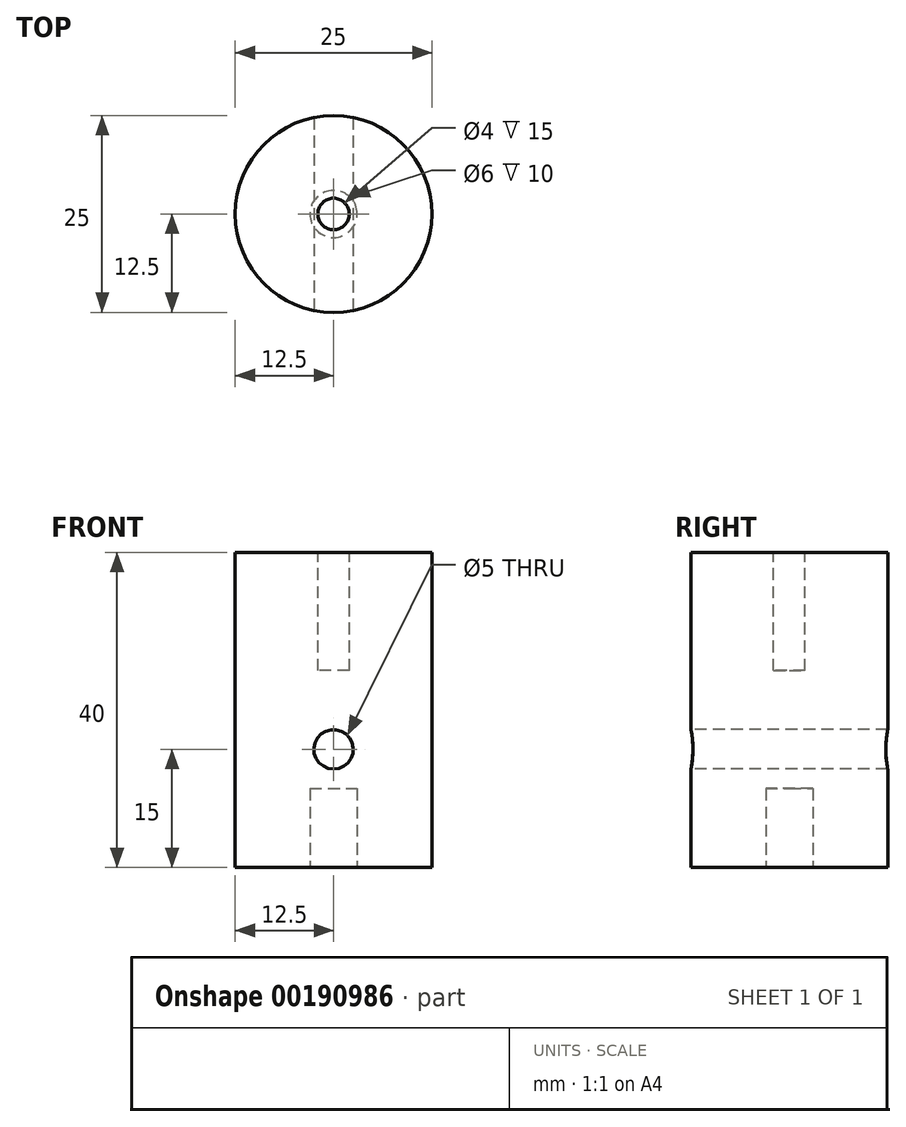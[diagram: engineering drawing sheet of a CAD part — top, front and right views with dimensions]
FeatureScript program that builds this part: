
annotation { "Feature Type Name" : "Feature", "Feature Type Description" : "" }
export const myFeature = defineFeature(function(context is Context, id is Id, definition is map)
    precondition{}
    {
        {
            var Q0;
            Q0=qCreatedBy(makeId("Top.planeOp"),FACE);
            var sketch = newSketch(context, id + "F0", { "sketchPlane" : qUnion([Q0])});
            skCircle(sketch, "E0", {"center": v(0, 0) * mm, "radius": 12.5 * mm});
            skSolve(sketch);
        }
        {
            var Q0;
            Q0 = qSketchRegion(id + "F0", true);
            extrude(context, id + "F1", {"entities" : qUnion([Q0]), "depth" : 40 * mm});
        }
        {
            var Q0;
            Q0=makeQuery(id+"F1.opExtrude","CAP_FACE",FACE,{"disambiguationData":[OSD([sQuery(id+"F0.wireOp",EDGE,"E0")])],"isStart":false});
            var sketch = newSketch(context, id + "F2", { "sketchPlane" : qUnion([Q0])});
            skCircle(sketch, "E1", {"center": v(0, 0) * mm, "radius": 2 * mm});
            skSolve(sketch);
        }
        {
            var Q0;
            Q0 = qSketchRegion(id + "F2", true);
            extrude(context, id + "F3", {"entities" : qUnion([Q0]), "operationType" : NewBodyOperationType.REMOVE, "oppositeDirection" : true, "depth" : 15 * mm});
        }
        {
            var Q0;
            Q0=makeQuery(id+"F1.opExtrude","CAP_FACE",FACE,{"disambiguationData":[OSD([sQuery(id+"F0.wireOp",EDGE,"E0")])],"isStart":true});
            var sketch = newSketch(context, id + "F4", { "sketchPlane" : qUnion([Q0])});
            skCircle(sketch, "E2", {"center": v(0, 0) * mm, "radius": 3 * mm});
            skSolve(sketch);
        }
        {
            var Q0;
            Q0 = qSketchRegion(id + "F4", true);
            extrude(context, id + "F5", {"entities" : qUnion([Q0]), "operationType" : NewBodyOperationType.REMOVE, "oppositeDirection" : true, "depth" : 10 * mm});
        }
        {
            var Q0;
            Q0=qCreatedBy(makeId("Front.planeOp"),FACE);
            var sketch = newSketch(context, id + "F6", { "sketchPlane" : qUnion([Q0])});
            skCircle(sketch, "E3", {"center": v(0, 15) * mm, "radius": 2.5 * mm});
            skSolve(sketch);
        }
        {
            var Q0;
            Q0 = qSketchRegion(id + "F6", true);
            extrude(context, id + "F7", {"entities" : qUnion([Q0]), "operationType" : NewBodyOperationType.REMOVE, "endBound" : BoundingType.SYMMETRIC, "oppositeDirection" : true, "depth" : 25 * mm});
        }
    });
